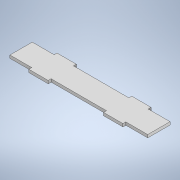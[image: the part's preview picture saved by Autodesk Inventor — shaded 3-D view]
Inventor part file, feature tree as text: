
AUTODESK INVENTOR PART (.ipt)
format: ipt  version: 2022 (Build 260153000, 153)  size: 124,928 bytes
history: native  units: in
note: dims shown in document units (in); Inventor stores cm internally (conversion verified against a paired STEP export)
features: extrude x1, sketch x1
ambient origin geometry x8: Origin, YZ Plane, XZ Plane, XY Plane, X Axis, Y Axis, Z Axis, Center Point
bodies: Solid1 (feature_tree)
feature tree (2):
  extrude  "Extrusion1"  Depth=5.5906in
  sketch  "Sketch1"  dims[d0=0.9055in d1=5.5906in d2=0.1181in d3=0.7874in d4=0.1181in d5=0.7874in d6=0.1181in d7=1.5157in d8=0.7874in d10=3.0315in d11=0.3937in d13=0.3937in d15=0.1181in d16=0.0in]
